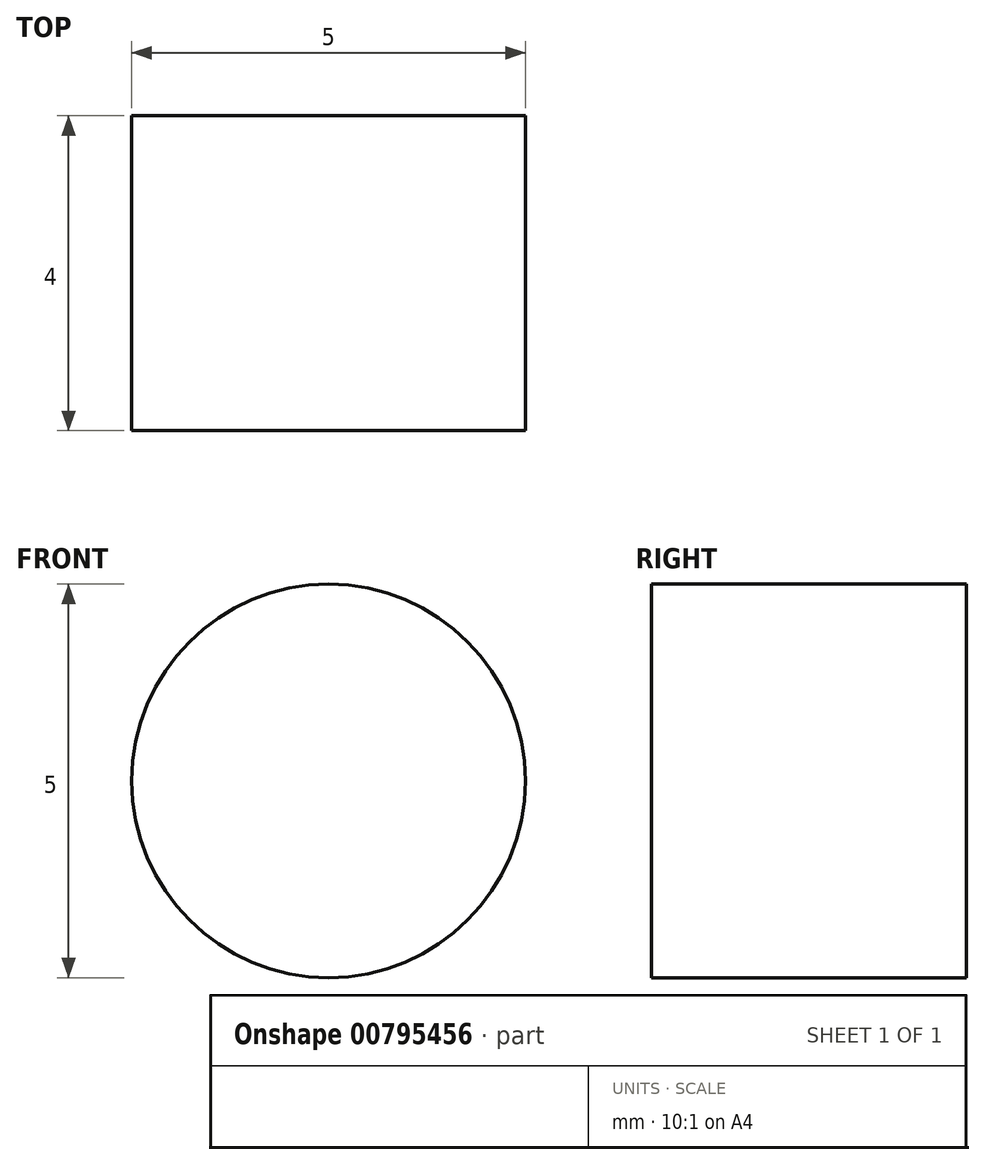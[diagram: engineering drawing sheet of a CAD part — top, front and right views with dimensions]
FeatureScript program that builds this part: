
annotation { "Feature Type Name" : "Feature", "Feature Type Description" : "" }
export const myFeature = defineFeature(function(context is Context, id is Id, definition is map)
    precondition{}
    {
        {
            var Q0;
            Q0=qCreatedBy(makeId("Front.planeOp"),FACE);
            var sketch = newSketch(context, id + "F0", { "sketchPlane" : qUnion([Q0])});
            skCircle(sketch, "E0", {"center": v(0, 0) * mm, "radius": 2.5 * mm});
            skSolve(sketch);
        }
        {
            var Q0;
            Q0=qSketchRegion(id+"F0",true);
            extrude(context, id + "F1", {"entities" : qUnion([Q0]), "depth" : 4 * mm, "offsetDistance" : 25 * mm});
        }
    });
